# Revit family: Roxtec H4 UG seals
name_source: partatom
category: Duct Accessories
revit_build: Autodesk Revit 2017 (Build: 20190508_0315(x64)
units: mm (PartAtom-declared; Revit-internal decimal feet)

## family parameters
Cut with Voids When Loaded = No
Host = Face
Part Type = Attaches To
Round Connector Dimension = Use Diameter
Shared = No

## types (2) — shared parameters
Core material = Roxylon black
Description = Sealing solutions for cables and pipes
ETIM Classification = EC000220
Fitting height = 69 mm  [stored 0.226378 ft]
Fitting material = Steel
Fitting thickness = 5 mm  [stored 0.0164042 ft]
Frame material = Roxylon black
Manufacturer = Roxtec
Sealing material = Roxylon black
URL = https://www.roxtec.com
Version = 2.0
zero-valued in all types: Default Elevation, NominalDepth, NominalHeight

## per-type parameters (varying)
| type | Front fitting diameter | Max cable Ø | Min cable Ø | Wall opening diameter | phase down distance | phase left right distance | phase left right height |
| H4-150 UG | 160 mm  [stored 0.524934 ft] | 54 mm | 30 mm  [stored 0.0984252 ft] | 150 mm | 34 mm | 39 mm | 14 mm  [stored 0.0459318 ft] |
| H4-200 UG | 210 mm  [stored 0.688976 ft] | 66 mm  [stored 0.216535 ft] | 50 mm  [stored 0.164042 ft] | 200 mm  [stored 0.656168 ft] | 48 mm  [stored 0.15748 ft] | 49 mm  [stored 0.160761 ft] | 18 mm  [stored 0.0590551 ft] |

note: [stored X ft] marks values corroborated as IEEE doubles in the binary element streams (Revit-internal decimal feet)

## geometry (parser evidence)
native form markers: Sweep x2
no freeform markers — native parametric forms only
